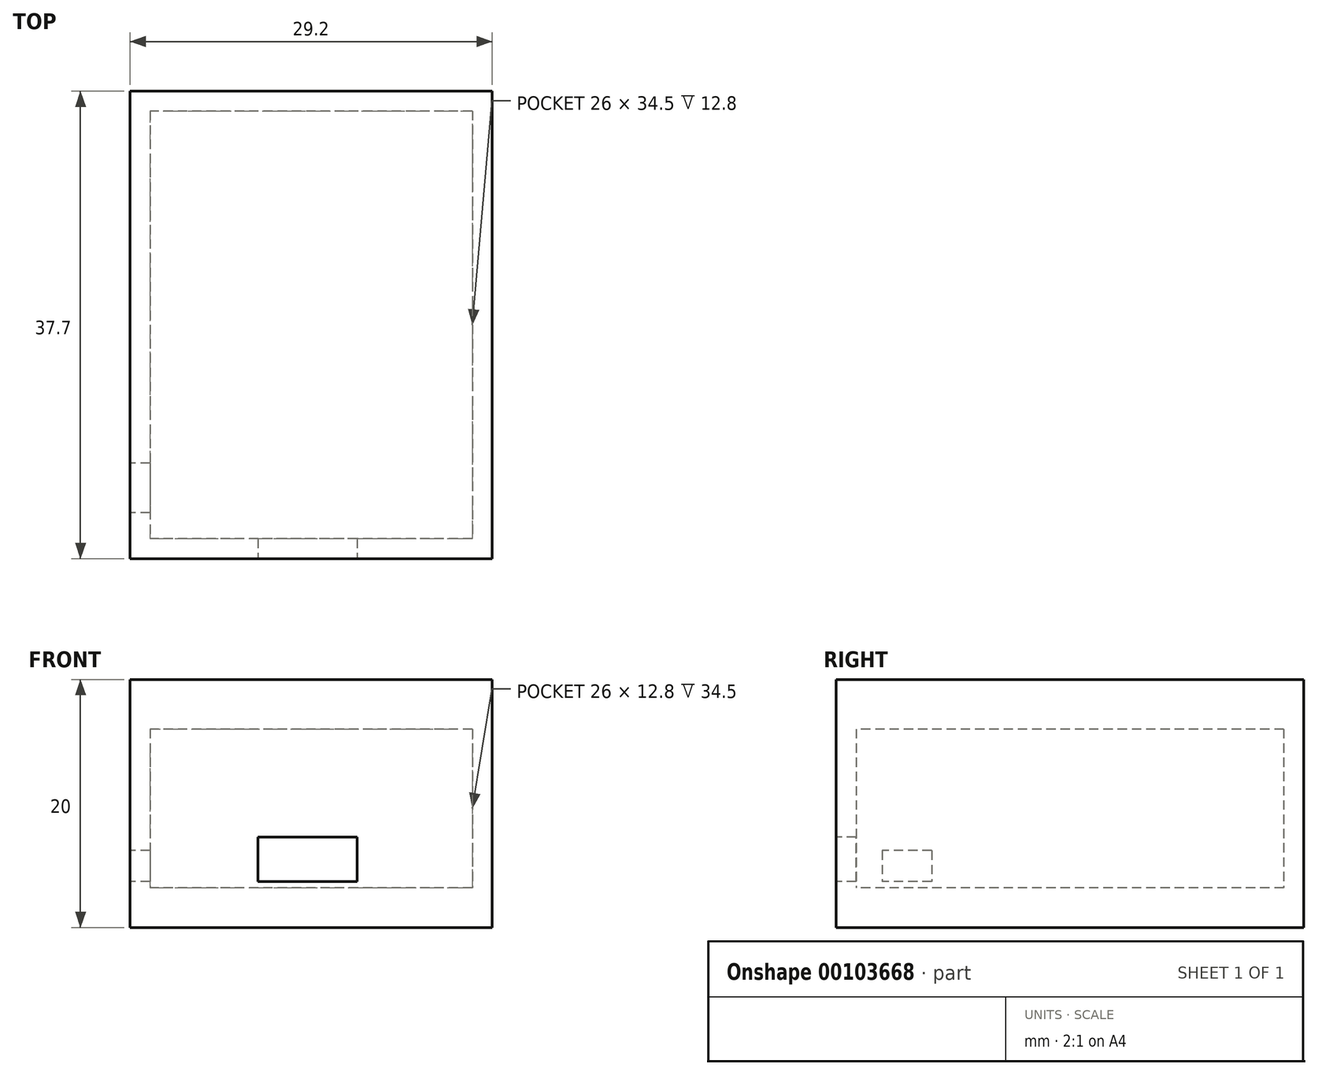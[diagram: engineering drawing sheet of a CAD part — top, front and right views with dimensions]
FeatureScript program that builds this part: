
annotation { "Feature Type Name" : "Feature", "Feature Type Description" : "" }
export const myFeature = defineFeature(function(context is Context, id is Id, definition is map)
    precondition{}
    {
        {
            var Q0;
            Q0=qCreatedBy(makeId("Top.planeOp"),FACE);
            var sketch = newSketch(context, id + "F0", { "sketchPlane" : qUnion([Q0])});
            skLineSegment(sketch, "E0.bottom", {"start": v(14.6, 18.85) * mm, "end": v(-14.6, 18.85) * mm});
            skLineSegment(sketch, "E0.top", {"start": v(14.6, -18.85) * mm, "end": v(-14.6, -18.85) * mm});
            skLineSegment(sketch, "E0.left", {"start": v(14.6, 18.85) * mm, "end": v(14.6, -18.85) * mm});
            skLineSegment(sketch, "E0.right", {"start": v(-14.6, 18.85) * mm, "end": v(-14.6, -18.85) * mm});
            skPoint(sketch, "E0.middle", {"position": v(0, 0) * mm});
            skSolve(sketch);
        }
        {
            var Q0;
            Q0=makeQuery(id+"F0.imprint","IMPRINT",FACE,{"disambiguationData":[TD([[makeQuery(id+"F0.imprint","IMPRINT",EDGE,{"derivedFrom":sQuery(id+"F0.wireOp",EDGE,"E0.bottom")}),1.0]])]});
            extrude(context, id + "F1", {"entities" : qUnion([Q0]), "depth" : 18 * mm});
        }
        {
            var Q0;
            Q0=makeQuery(id+"F1.opExtrude","CAP_FACE",FACE,{"disambiguationData":[OSD([sQuery(id+"F0.wireOp",EDGE,"E0.bottom"),sQuery(id+"F0.wireOp",EDGE,"E0.top"),sQuery(id+"F0.wireOp",EDGE,"E0.left"),sQuery(id+"F0.wireOp",EDGE,"E0.right")])],"isStart":false});
            shell(context, id + "F2", {"entities" : qUnion([Q0]), "thickness" : 1.6 * mm});
        }
        {
            var Q0;
            Q0=makeQuery(id+"F1.opExtrude","SWEPT_FACE",FACE,{"disambiguationData":[OSD([sQuery(id+"F0.wireOp",EDGE,"E0.top")])]});
            var sketch = newSketch(context, id + "F3", { "sketchPlane" : qUnion([Q0])});
            skLineSegment(sketch, "E1.bottom", {"start": v(-4.3, 7.3) * mm, "end": v(3.7, 7.3) * mm});
            skLineSegment(sketch, "E1.top", {"start": v(-4.3, 3.7) * mm, "end": v(3.7, 3.7) * mm});
            skLineSegment(sketch, "E1.left", {"start": v(-4.3, 7.3) * mm, "end": v(-4.3, 3.7) * mm});
            skLineSegment(sketch, "E1.right", {"start": v(3.7, 7.3) * mm, "end": v(3.7, 3.7) * mm});
            skPoint(sketch, "E2.endSnap0", {"position": v(0, 0) * mm});
            skPoint(sketch, "E3", {"position": v(-0.3, 7.3) * mm});
            skLineSegment(sketch, "E4", {"start": v(-2.82, 0) * mm, "end": v(-2.82, 3.7) * mm, "construction": true});
            skLineSegment(sketch, "E5", {"start": v(-4.3, 3.7) * mm, "end": v(-14.6, 3.7) * mm, "construction": true});
            skSolve(sketch);
        }
        {
            var Q0;
            Q0=makeQuery(id+"F3.imprint","IMPRINT",FACE,{"disambiguationData":[TD([[makeQuery(id+"F3.imprint","IMPRINT",EDGE,{"derivedFrom":sQuery(id+"F3.wireOp",EDGE,"E1.bottom")}),-1.0]])]});
            var Q1;
            Q1=makeQuery(id+"F2.opShell","OFFSET_FACE",FACE,{"disambiguationData":[OSD([sQuery(id+"F0.wireOp",EDGE,"E0.top")])]});
            extrude(context, id + "F4", {"entities" : qUnion([Q0]), "operationType" : NewBodyOperationType.REMOVE, "endBound" : BoundingType.UP_TO_SURFACE, "oppositeDirection" : true, "endBoundEntityFace" : qUnion([Q1]), "depth" : 25 * mm});
        }
        {
            var Q0;
            Q0=makeQuery(id+"F1.opExtrude","SWEPT_FACE",FACE,{"disambiguationData":[OSD([sQuery(id+"F0.wireOp",EDGE,"E0.right")])]});
            var sketch = newSketch(context, id + "F5", { "sketchPlane" : qUnion([Q0])});
            skLineSegment(sketch, "E6.bottom", {"start": v(11.15, 6.2) * mm, "end": v(15.15, 6.2) * mm});
            skLineSegment(sketch, "E6.top", {"start": v(11.15, 3.7) * mm, "end": v(15.15, 3.7) * mm});
            skLineSegment(sketch, "E6.left", {"start": v(11.15, 6.2) * mm, "end": v(11.15, 3.7) * mm});
            skLineSegment(sketch, "E6.right", {"start": v(15.15, 6.2) * mm, "end": v(15.15, 3.7) * mm});
            skLineSegment(sketch, "E7", {"start": v(15.15, 3.7) * mm, "end": v(18.85, 3.7) * mm, "construction": true});
            skLineSegment(sketch, "E8", {"start": v(15.15, 3.7) * mm, "end": v(15.15, 0) * mm, "construction": true});
            skSolve(sketch);
        }
        {
            var Q0;
            Q0=makeQuery(id+"F5.imprint","IMPRINT",FACE,{"disambiguationData":[TD([[makeQuery(id+"F5.imprint","IMPRINT",EDGE,{"derivedFrom":sQuery(id+"F5.wireOp",EDGE,"E6.bottom")}),-1.0]])]});
            var Q1;
            Q1=makeQuery(id+"F2.opShell","OFFSET_FACE",FACE,{"disambiguationData":[OSD([sQuery(id+"F0.wireOp",EDGE,"E0.right")])]});
            extrude(context, id + "F6", {"entities" : qUnion([Q0]), "operationType" : NewBodyOperationType.REMOVE, "endBound" : BoundingType.UP_TO_SURFACE, "oppositeDirection" : true, "endBoundEntityFace" : qUnion([Q1]), "depth" : 25 * mm});
        }
        {
            var Q0;
            Q0=makeQuery(id+"F2.opShell","OFFSET_FACE",FACE,{"disambiguationData":[OSD([sQuery(id+"F0.wireOp",EDGE,"E0.bottom"),sQuery(id+"F0.wireOp",EDGE,"E0.top"),sQuery(id+"F0.wireOp",EDGE,"E0.left"),sQuery(id+"F0.wireOp",EDGE,"E0.right")])]});
            var sketch = newSketch(context, id + "F7", { "sketchPlane" : qUnion([Q0])});
            skLineSegment(sketch, "E9.bottom", {"start": v(-13, 17.25) * mm, "end": v(13, 17.25) * mm});
            skLineSegment(sketch, "E9.top", {"start": v(-13, -17.25) * mm, "end": v(13, -17.25) * mm});
            skLineSegment(sketch, "E9.left", {"start": v(-13, 17.25) * mm, "end": v(-13, -17.25) * mm});
            skLineSegment(sketch, "E9.right", {"start": v(13, 17.25) * mm, "end": v(13, -17.25) * mm});
            skSolve(sketch);
        }
        {
            var Q0;
            Q0=makeQuery(id+"F7.imprint","IMPRINT",FACE,{"disambiguationData":[TD([[makeQuery(id+"F7.imprint","IMPRINT",EDGE,{"derivedFrom":sQuery(id+"F7.wireOp",EDGE,"E9.bottom")}),1.0]])]});
            extrude(context, id + "F8", {"entities" : qUnion([Q0]), "operationType" : NewBodyOperationType.ADD, "depth" : 1.6 * mm});
        }
        {
            var Q0;
            Q0=makeQuery(id+"F1.opExtrude","CAP_FACE",FACE,{"disambiguationData":[OSD([sQuery(id+"F0.wireOp",EDGE,"E0.bottom"),sQuery(id+"F0.wireOp",EDGE,"E0.top"),sQuery(id+"F0.wireOp",EDGE,"E0.left"),sQuery(id+"F0.wireOp",EDGE,"E0.right")])],"isStart":false});
            var sketch = newSketch(context, id + "F9", { "sketchPlane" : qUnion([Q0])});
            skLineSegment(sketch, "E10.bottom", {"start": v(-14.6, 18.85) * mm, "end": v(14.6, 18.85) * mm});
            skLineSegment(sketch, "E10.top", {"start": v(-14.6, -18.85) * mm, "end": v(14.6, -18.85) * mm});
            skLineSegment(sketch, "E10.left", {"start": v(-14.6, 18.85) * mm, "end": v(-14.6, -18.85) * mm});
            skLineSegment(sketch, "E10.right", {"start": v(14.6, 18.85) * mm, "end": v(14.6, -18.85) * mm});
            skLineSegment(sketch, "E11.bottom", {"start": v(13, -17.25) * mm, "end": v(-13, -17.25) * mm, "construction": true});
            skLineSegment(sketch, "E11.top", {"start": v(13, 17.25) * mm, "end": v(-13, 17.25) * mm, "construction": true});
            skLineSegment(sketch, "E11.left", {"start": v(13, -17.25) * mm, "end": v(13, 17.25) * mm, "construction": true});
            skLineSegment(sketch, "E11.right", {"start": v(-13, -17.25) * mm, "end": v(-13, 17.25) * mm, "construction": true});
            skSolve(sketch);
        }
        {
            var Q0;
            Q0 = qSketchRegion(id + "F9", true);
            extrude(context, id + "F10", {"entities" : qUnion([Q0]), "depth" : 2 * mm});
        }
        {
            var Q0;
            {var subQ0=sQuery(id+"F0.wireOp",EDGE,"E0.bottom");Q0=makeQuery(id+"F9.imprint","IMPRINT",FACE,{"disambiguationData":[TD([[makeQuery(id+"F9.imprint","IMPRINT",EDGE,{"derivedFrom":makeQuery(id+"F2.opShell","OFFSET_EDGE",EDGE,{"disambiguationData":[OSD([subQ0]),TDD([makeQuery(id+"F1.opExtrude","CAP_EDGE",EDGE,{"disambiguationData":[OSD([subQ0])],"isStart":false})])]})}),1.0]])]});}
            extrude(context, id + "F11", {"entities" : qUnion([Q0]), "operationType" : NewBodyOperationType.ADD, "oppositeDirection" : true, "depth" : 2 * mm});
        }
    });
